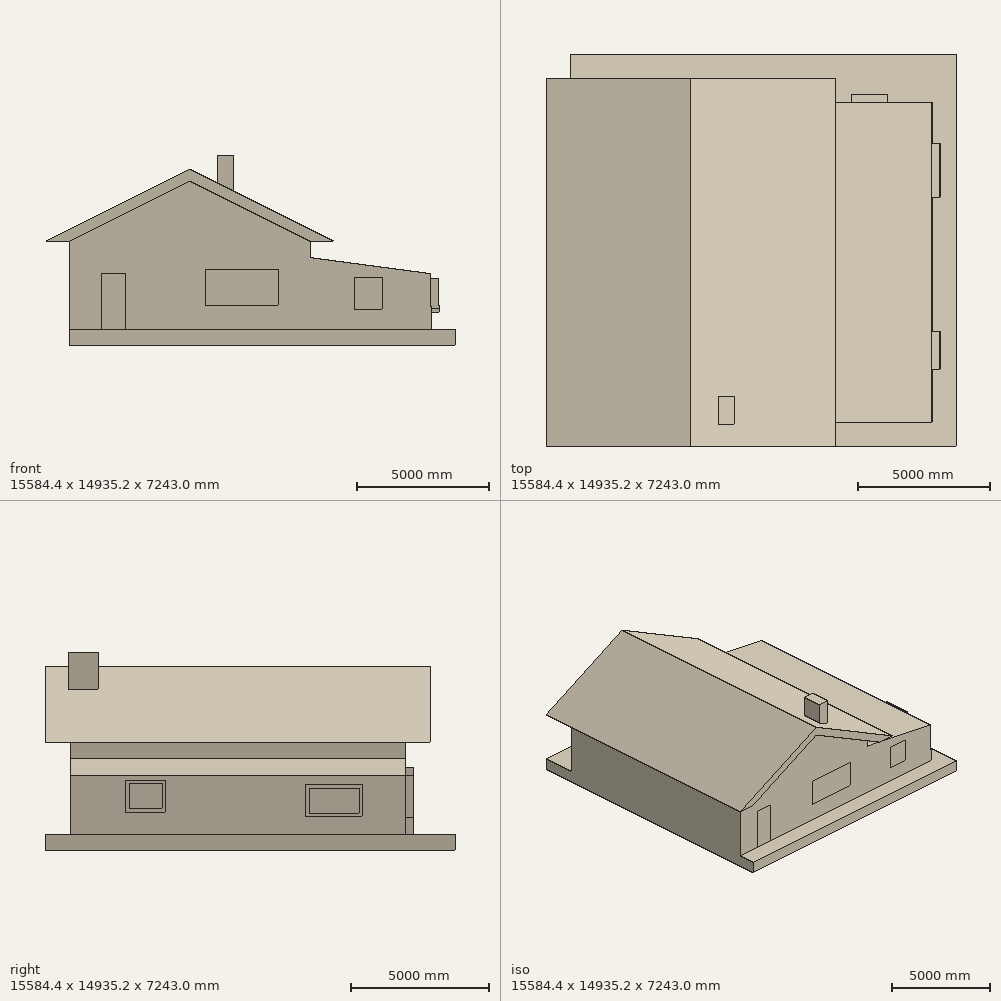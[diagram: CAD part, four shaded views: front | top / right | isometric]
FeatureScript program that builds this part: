
annotation { "Feature Type Name" : "Feature", "Feature Type Description" : "" }
export const myFeature = defineFeature(function(context is Context, id is Id, definition is map)
    precondition{}
    {
        {
            var Q0;
            Q0=qCreatedBy(makeId("Front.planeOp"),FACE);
            var sketch = newSketch(context, id + "F0", { "sketchPlane" : qUnion([Q0])});
            skLineSegment(sketch, "E0", {"start": v(0, 0) * mm, "end": v(-4572, 0) * mm});
            skLineSegment(sketch, "E1", {"start": v(0, 0) * mm, "end": v(4572, 0) * mm});
            skLineSegment(sketch, "E2", {"start": v(-4572, 0) * mm, "end": v(0, 2286) * mm});
            skLineSegment(sketch, "E3", {"start": v(0, 2286) * mm, "end": v(4572, 0) * mm});
            skLineSegment(sketch, "E4", {"start": v(0, 2286) * mm, "end": v(0, 2743.2) * mm});
            skLineSegment(sketch, "E5", {"start": v(-4572, 0) * mm, "end": v(-5486.4, 0) * mm});
            skLineSegment(sketch, "E6", {"start": v(4572, 0) * mm, "end": v(5486.4, 0) * mm});
            skLineSegment(sketch, "E7", {"start": v(0, 2286) * mm, "end": v(0, 0) * mm});
            skLineSegment(sketch, "E8", {"start": v(-5486.4, 0) * mm, "end": v(0, 2743.2) * mm});
            skLineSegment(sketch, "E9", {"start": v(0, 2743.2) * mm, "end": v(5486.4, 0) * mm});
            skLineSegment(sketch, "E10.bottom", {"start": v(-4572, 0) * mm, "end": v(4572, 0) * mm});
            skLineSegment(sketch, "E10.top", {"start": v(-4572, -3352.8) * mm, "end": v(4572, -3352.8) * mm});
            skLineSegment(sketch, "E10.left", {"start": v(-4572, 0) * mm, "end": v(-4572, -3352.8) * mm});
            skLineSegment(sketch, "E10.right", {"start": v(4572, 0) * mm, "end": v(4572, -3352.8) * mm});
            skLineSegment(sketch, "E11", {"start": v(-4572, -3352.8) * mm, "end": v(-4572, -3962.4) * mm});
            skLineSegment(sketch, "E12", {"start": v(-4572, -3962.4) * mm, "end": v(4572, -3962.4) * mm});
            skLineSegment(sketch, "E13", {"start": v(4572, -3962.4) * mm, "end": v(4572, -3352.8) * mm});
            skLineSegment(sketch, "E14", {"start": v(-3352.8, -3352.8) * mm, "end": v(-3352.8, -1219.2) * mm});
            skLineSegment(sketch, "E15", {"start": v(-3352.8, -1219.2) * mm, "end": v(-2438.4, -1219.2) * mm});
            skLineSegment(sketch, "E16", {"start": v(-2438.4, -1219.2) * mm, "end": v(-2438.4, -3352.8) * mm});
            skLineSegment(sketch, "E17.0", {"start": v(-2133.6, -914.4) * mm, "end": v(-2133.6, -3352.8) * mm});
            skLineSegment(sketch, "E17.1", {"start": v(-3657.6, -914.4) * mm, "end": v(-2133.6, -914.4) * mm});
            skLineSegment(sketch, "E17.2", {"start": v(-3657.6, -3352.8) * mm, "end": v(-3657.6, -914.4) * mm});
            skLineSegment(sketch, "E18.bottom", {"start": v(609.6, -1066.8) * mm, "end": v(3352.8, -1066.8) * mm});
            skLineSegment(sketch, "E18.top", {"start": v(609.6, -2438.4) * mm, "end": v(3352.8, -2438.4) * mm});
            skLineSegment(sketch, "E18.left", {"start": v(609.6, -1066.8) * mm, "end": v(609.6, -2438.4) * mm});
            skLineSegment(sketch, "E18.right", {"start": v(3352.8, -1066.8) * mm, "end": v(3352.8, -2438.4) * mm});
            skLineSegment(sketch, "E19.0", {"start": v(457.2, -914.4) * mm, "end": v(3505.2, -914.4) * mm});
            skLineSegment(sketch, "E19.1", {"start": v(457.2, -914.4) * mm, "end": v(457.2, -2590.8) * mm});
            skLineSegment(sketch, "E19.2", {"start": v(457.2, -2590.8) * mm, "end": v(3505.2, -2590.8) * mm});
            skLineSegment(sketch, "E19.3", {"start": v(3505.2, -914.4) * mm, "end": v(3505.2, -2590.8) * mm});
            skLineSegment(sketch, "E20.bottom", {"start": v(4572, -3962.4) * mm, "end": v(9183.62, -3962.4) * mm});
            skLineSegment(sketch, "E20.top", {"start": v(4572, -3962.4) * mm, "end": v(9183.62, -3962.4) * mm});
            skLineSegment(sketch, "E20.left", {"start": v(4572, -3962.4) * mm, "end": v(4572, -3962.4) * mm});
            skLineSegment(sketch, "E20.right", {"start": v(9183.62, -3962.4) * mm, "end": v(9183.62, -3962.4) * mm});
            skLineSegment(sketch, "E21", {"start": v(4572, -3352.8) * mm, "end": v(9183.62, -3352.8) * mm});
            skLineSegment(sketch, "E22", {"start": v(9183.62, -3352.8) * mm, "end": v(9183.62, -3962.4) * mm});
            skLineSegment(sketch, "E23", {"start": v(9131.61, -610.1) * mm, "end": v(9183.62, -3352.8) * mm});
            skLineSegment(sketch, "E24", {"start": v(9131.61, -610.1) * mm, "end": v(9143.17, -1219.58) * mm});
            skLineSegment(sketch, "E25", {"start": v(4572, 0) * mm, "end": v(9131.61, -610.1) * mm});
            skLineSegment(sketch, "E26", {"start": v(9143.17, -1219.58) * mm, "end": v(4572, -610.1) * mm});
            skPoint(sketch, "E27.firstSnap0", {"position": v(3505.2, -1752.6) * mm});
            skLineSegment(sketch, "E27.bottom", {"start": v(6096, -1211.42) * mm, "end": v(7467.6, -1211.42) * mm});
            skLineSegment(sketch, "E27.top", {"start": v(6096, -2735.42) * mm, "end": v(7467.6, -2735.42) * mm});
            skLineSegment(sketch, "E27.left", {"start": v(6096, -1211.42) * mm, "end": v(6096, -2735.42) * mm});
            skLineSegment(sketch, "E27.right", {"start": v(7467.6, -1211.42) * mm, "end": v(7467.6, -2735.42) * mm});
            skLineSegment(sketch, "E28.0", {"start": v(6248.4, -1363.82) * mm, "end": v(7315.2, -1363.82) * mm});
            skLineSegment(sketch, "E28.1", {"start": v(6248.4, -1363.82) * mm, "end": v(6248.4, -2583.02) * mm});
            skLineSegment(sketch, "E28.2", {"start": v(6248.4, -2583.02) * mm, "end": v(7315.2, -2583.02) * mm});
            skLineSegment(sketch, "E28.3", {"start": v(7315.2, -1363.82) * mm, "end": v(7315.2, -2583.02) * mm});
            skLineSegment(sketch, "E29", {"start": v(1058.81, 2213.8) * mm, "end": v(1058.81, 3280.6) * mm});
            skLineSegment(sketch, "E30", {"start": v(1058.81, 3280.6) * mm, "end": v(1668.41, 3280.6) * mm});
            skLineSegment(sketch, "E31", {"start": v(1668.41, 3280.6) * mm, "end": v(1668.41, 1909) * mm});
            skSolve(sketch);
        }
        {
            var Q0;
            Q0=makeQuery(id+"F0.imprint","IMPRINT",FACE,{"disambiguationData":[TD([[makeQuery(id+"F0.imprint","IMPRINT",EDGE,{"derivedFrom":sQuery(id+"F0.wireOp",EDGE,"E2")}),1.0]])]});
            var Q1;
            Q1=makeQuery(id+"F0.imprint","IMPRINT",FACE,{"disambiguationData":[TD([[makeQuery(id+"F0.imprint","IMPRINT",EDGE,{"derivedFrom":sQuery(id+"F0.wireOp",EDGE,"E3")}),1.0]])]});
            var Q2;
            Q2=makeQuery(id+"F0.imprint","IMPRINT",FACE,{"disambiguationData":[TD([[makeQuery(id+"F0.imprint","IMPRINT",EDGE,{"derivedFrom":sQuery(id+"F0.wireOp",EDGE,"E24")}),-1.0]])]});
            extrude(context, id + "F1", {"entities" : qUnion([Q0, Q1, Q2]), "depth" : 914.4 * mm, "offsetDistance" : 30.48 * mm, "hasSecondDirection" : true, "secondDirectionOppositeDirection" : true, "secondDirectionDepth" : 13106.4 * mm});
        }
        {
            var Q0;
            {var subQ0=sQuery(id+"F0.wireOp",EDGE,"E2");Q0=makeQuery(id+"F0.imprint","IMPRINT",FACE,{"disambiguationData":[TD([[makeQuery(id+"F0.imprint","IMPRINT",EDGE,{"derivedFrom":subQ0}),-1.0]])]});}
            var Q1;
            {var subQ0=sQuery(id+"F0.wireOp",EDGE,"E3");Q1=makeQuery(id+"F0.imprint","IMPRINT",FACE,{"disambiguationData":[TD([[makeQuery(id+"F0.imprint","IMPRINT",EDGE,{"derivedFrom":subQ0}),-1.0]])]});}
            var Q2;
            {var subQ8=sQuery(id+"F0.wireOp",EDGE,"E10.left");Q2=makeQuery(id+"F0.imprint","IMPRINT",FACE,{"disambiguationData":[TD([[makeQuery(id+"F0.imprint","IMPRINT",EDGE,{"derivedFrom":subQ8}),1.0]])]});}
            var Q3;
            {var subQ5=sQuery(id+"F0.wireOp",EDGE,"E11");Q3=makeQuery(id+"F0.imprint","IMPRINT",FACE,{"disambiguationData":[TD([[makeQuery(id+"F0.imprint","IMPRINT",EDGE,{"derivedFrom":subQ5}),1.0]])]});}
            extrude(context, id + "F2", {"entities" : qUnion([Q0, Q1, Q2, Q3]), "operationType" : NewBodyOperationType.ADD, "depth" : 0 * mm, "offsetDistance" : 30.48 * mm, "hasSecondDirection" : true, "secondDirectionOppositeDirection" : true, "secondDirectionDepth" : 12192 * mm});
        }
        {
            var Q0;
            {var subQ5=sQuery(id+"F0.wireOp",EDGE,"E11");Q0=makeQuery(id+"F0.imprint","IMPRINT",FACE,{"disambiguationData":[TD([[makeQuery(id+"F0.imprint","IMPRINT",EDGE,{"derivedFrom":subQ5}),1.0]])]});}
            var Q1;
            Q1=makeQuery(id+"F0.imprint","IMPRINT",FACE,{"disambiguationData":[TD([[makeQuery(id+"F0.imprint","IMPRINT",EDGE,{"derivedFrom":sQuery(id+"F0.wireOp",EDGE,"E13")}),-1.0]])]});
            extrude(context, id + "F3", {"entities" : qUnion([Q0, Q1]), "operationType" : NewBodyOperationType.ADD, "depth" : 914.4 * mm, "offsetDistance" : 30.48 * mm, "hasSecondDirection" : true, "secondDirectionOppositeDirection" : true, "secondDirectionDepth" : 14020.8 * mm});
        }
        {
            var Q0;
            {var subQ1=sQuery(id+"F0.wireOp",EDGE,"E21");Q0=makeQuery(id+"F0.imprint","IMPRINT",FACE,{"disambiguationData":[TD([[makeQuery(id+"F0.imprint","IMPRINT",EDGE,{"derivedFrom":subQ1}),1.0]])]});}
            extrude(context, id + "F4", {"entities" : qUnion([Q0]), "depth" : -12192 * mm, "offsetDistance" : 30.48 * mm});
        }
        {
            var Q0;
            Q0=makeQuery(id+"F3.opExtrude","SWEPT_FACE",FACE,{"disambiguationData":[OSD([sQuery(id+"F0.wireOp",EDGE,"E22")])]});
            extrude(context, id + "F5", {"entities" : qUnion([Q0]), "operationType" : NewBodyOperationType.ADD, "depth" : 914.4 * mm, "offsetDistance" : 30.48 * mm});
        }
        {
            var Q0;
            {var subQ0=sQuery(id+"F0.wireOp",EDGE,"E14");Q0=makeQuery(id+"F0.imprint","IMPRINT",FACE,{"disambiguationData":[TD([[makeQuery(id+"F0.imprint","IMPRINT",EDGE,{"derivedFrom":subQ0}),1.0]])]});}
            var Q1;
            Q1=makeQuery(id+"F0.imprint","IMPRINT",FACE,{"disambiguationData":[TD([[makeQuery(id+"F0.imprint","IMPRINT",EDGE,{"derivedFrom":sQuery(id+"F0.wireOp",EDGE,"E18.bottom")}),1.0]])]});
            var Q2;
            Q2=makeQuery(id+"F0.imprint","IMPRINT",FACE,{"disambiguationData":[TD([[makeQuery(id+"F0.imprint","IMPRINT",EDGE,{"derivedFrom":sQuery(id+"F0.wireOp",EDGE,"E27.bottom")}),-1.0]])]});
            extrude(context, id + "F6", {"entities" : qUnion([Q0, Q1, Q2]), "operationType" : NewBodyOperationType.ADD, "depth" : 0 * mm, "offsetDistance" : 30.48 * mm, "hasSecondDirection" : true, "secondDirectionOppositeDirection" : true, "secondDirectionDepth" : 12496.8 * mm});
        }
        {
            var Q0;
            {var subQ0=sQuery(id+"F0.wireOp",EDGE,"E14");Q0=makeQuery(id+"F0.imprint","IMPRINT",FACE,{"disambiguationData":[TD([[makeQuery(id+"F0.imprint","IMPRINT",EDGE,{"derivedFrom":subQ0}),-1.0]])]});}
            var Q1;
            Q1=makeQuery(id+"F0.imprint","IMPRINT",FACE,{"disambiguationData":[TD([[makeQuery(id+"F0.imprint","IMPRINT",EDGE,{"derivedFrom":sQuery(id+"F0.wireOp",EDGE,"E18.bottom")}),-1.0]])]});
            var Q2;
            Q2=makeQuery(id+"F0.imprint","IMPRINT",FACE,{"disambiguationData":[TD([[makeQuery(id+"F0.imprint","IMPRINT",EDGE,{"derivedFrom":sQuery(id+"F0.wireOp",EDGE,"E28.0")}),-1.0]])]});
            extrude(context, id + "F7", {"entities" : qUnion([Q0, Q1, Q2]), "oppositeDirection" : true, "depth" : 12344.4 * mm, "offsetDistance" : 30.48 * mm});
        }
        {
            var Q0;
            Q0=makeQuery(id+"F4.opExtrude","SWEPT_FACE",FACE,{"disambiguationData":[OSD([sQuery(id+"F0.wireOp",EDGE,"E23")])]});
            var sketch = newSketch(context, id + "F8", { "sketchPlane" : qUnion([Q0])});
            skLineSegment(sketch, "E32.bottom", {"start": v(2133.6, -1697.52) * mm, "end": v(3352.8, -1697.52) * mm});
            skLineSegment(sketch, "E32.top", {"start": v(2133.6, -2611.92) * mm, "end": v(3352.8, -2611.92) * mm});
            skLineSegment(sketch, "E32.left", {"start": v(2133.6, -1697.52) * mm, "end": v(2133.6, -2611.92) * mm});
            skLineSegment(sketch, "E32.right", {"start": v(3352.8, -1697.52) * mm, "end": v(3352.8, -2611.92) * mm});
            skLineSegment(sketch, "E33.0", {"start": v(2011.68, -1575.6) * mm, "end": v(3474.72, -1575.6) * mm});
            skLineSegment(sketch, "E33.1", {"start": v(2011.68, -1575.6) * mm, "end": v(2011.68, -2733.84) * mm});
            skLineSegment(sketch, "E33.2", {"start": v(2011.68, -2733.84) * mm, "end": v(3474.72, -2733.84) * mm});
            skLineSegment(sketch, "E33.3", {"start": v(3474.72, -1575.6) * mm, "end": v(3474.72, -2733.84) * mm});
            skLineSegment(sketch, "E34.bottom", {"start": v(8686.8, -1849.92) * mm, "end": v(10515.6, -1849.92) * mm});
            skLineSegment(sketch, "E34.top", {"start": v(8686.8, -2764.32) * mm, "end": v(10515.6, -2764.32) * mm});
            skLineSegment(sketch, "E34.left", {"start": v(8686.8, -1849.92) * mm, "end": v(8686.8, -2764.32) * mm});
            skLineSegment(sketch, "E34.right", {"start": v(10515.6, -1849.92) * mm, "end": v(10515.6, -2764.32) * mm});
            skLineSegment(sketch, "E35.0", {"start": v(8564.88, -1728) * mm, "end": v(10637.52, -1728) * mm});
            skLineSegment(sketch, "E35.1", {"start": v(8564.88, -1728) * mm, "end": v(8564.88, -2886.24) * mm});
            skLineSegment(sketch, "E35.2", {"start": v(8564.88, -2886.24) * mm, "end": v(10637.52, -2886.24) * mm});
            skLineSegment(sketch, "E35.3", {"start": v(10637.52, -1728) * mm, "end": v(10637.52, -2886.24) * mm});
            skSolve(sketch);
        }
        {
            var Q0;
            Q0=makeQuery(id+"F8.imprint","IMPRINT",FACE,{"disambiguationData":[TD([[makeQuery(id+"F8.imprint","IMPRINT",EDGE,{"derivedFrom":sQuery(id+"F8.wireOp",EDGE,"E32.bottom")}),1.0]])]});
            var Q1;
            Q1=makeQuery(id+"F8.imprint","IMPRINT",FACE,{"disambiguationData":[TD([[makeQuery(id+"F8.imprint","IMPRINT",EDGE,{"derivedFrom":sQuery(id+"F8.wireOp",EDGE,"E34.bottom")}),1.0]])]});
            extrude(context, id + "F9", {"entities" : qUnion([Q0, Q1]), "operationType" : NewBodyOperationType.ADD, "depth" : 304.8 * mm, "offsetDistance" : 30.48 * mm});
        }
        {
            var Q0;
            Q0=makeQuery(id+"F9.boolean.opBoolean","SPLIT",FACE,{"disambiguationData":[TD([makeQuery(id+"F9.opExtrude","SWEPT_FACE",FACE,{"disambiguationData":[OSD([sQuery(id+"F8.wireOp",EDGE,"E34.bottom")])]})])],"derivedFrom":makeQuery(id+"F4.opExtrude","SWEPT_FACE",FACE,{"disambiguationData":[OSD([sQuery(id+"F0.wireOp",EDGE,"E23")])]})});
            var Q1;
            Q1=makeQuery(id+"F9.boolean.opBoolean","SPLIT",FACE,{"disambiguationData":[TD([makeQuery(id+"F9.opExtrude","SWEPT_FACE",FACE,{"disambiguationData":[OSD([sQuery(id+"F8.wireOp",EDGE,"E32.bottom")])]})])],"derivedFrom":makeQuery(id+"F4.opExtrude","SWEPT_FACE",FACE,{"disambiguationData":[OSD([sQuery(id+"F0.wireOp",EDGE,"E23")])]})});
            extrude(context, id + "F10", {"entities" : qUnion([Q0, Q1]), "operationType" : NewBodyOperationType.ADD, "depth" : 152.4 * mm, "offsetDistance" : 30.48 * mm});
        }
        {
            var Q0;
            {var subQ0=sQuery(id+"F0.wireOp",EDGE,"E29");Q0=makeQuery(id+"F0.imprint","IMPRINT",FACE,{"disambiguationData":[TD([[makeQuery(id+"F0.imprint","IMPRINT",EDGE,{"derivedFrom":subQ0}),-1.0]])]});}
            extrude(context, id + "F11", {"entities" : qUnion([Q0]), "operationType" : NewBodyOperationType.ADD, "depth" : 60.96 * mm, "offsetDistance" : 30.48 * mm, "hasSecondDirection" : true, "secondDirectionOppositeDirection" : true, "secondDirectionDepth" : 1005.84 * mm});
        }
        {
            var Q0;
            Q0=makeQuery(id+"F2.opExtrude","CAP_FACE",FACE,{"disambiguationData":[OSD([sQuery(id+"F0.wireOp",EDGE,"E2"),sQuery(id+"F0.wireOp",EDGE,"E3"),sQuery(id+"F0.wireOp",EDGE,"E10.top"),sQuery(id+"F0.wireOp",EDGE,"E10.left"),sQuery(id+"F0.wireOp",EDGE,"E10.right"),sQuery(id+"F0.wireOp",EDGE,"E11"),sQuery(id+"F0.wireOp",EDGE,"E12"),sQuery(id+"F0.wireOp",EDGE,"E13"),sQuery(id+"F0.wireOp",EDGE,"E17.0"),sQuery(id+"F0.wireOp",EDGE,"E17.1"),sQuery(id+"F0.wireOp",EDGE,"E17.2"),sQuery(id+"F0.wireOp",EDGE,"E19.0"),sQuery(id+"F0.wireOp",EDGE,"E19.1"),sQuery(id+"F0.wireOp",EDGE,"E19.2"),sQuery(id+"F0.wireOp",EDGE,"E19.3")])],"isStart":true});
            var sketch = newSketch(context, id + "F12", { "sketchPlane" : qUnion([Q0])});
            skText(sketch, "E36", { "text": "Owen W", "fontName": "OpenSans-Regular.ttf"});
            const initialGuessF12  = {"E36": [-8.48857, 3.78689, 1, 0, 2.17647]};
            skSetInitialGuess(sketch, initialGuessF12);
            skSolve(sketch);
        }
        {
            var Q0;
            Q0 = qConstructionFilter(qBodyType(qCreatedBy(id + "F12" ,EDGE), BodyType.WIRE), ConstructionObject.NO);
            extrude(context, id + "F13", {"bodyType" : ToolBodyType.SURFACE, "surfaceEntities" : qUnion([Q0]), "oppositeDirection" : true, "depth" : 1463.04 * mm, "offsetDistance" : 30.48 * mm});
        }
    });
